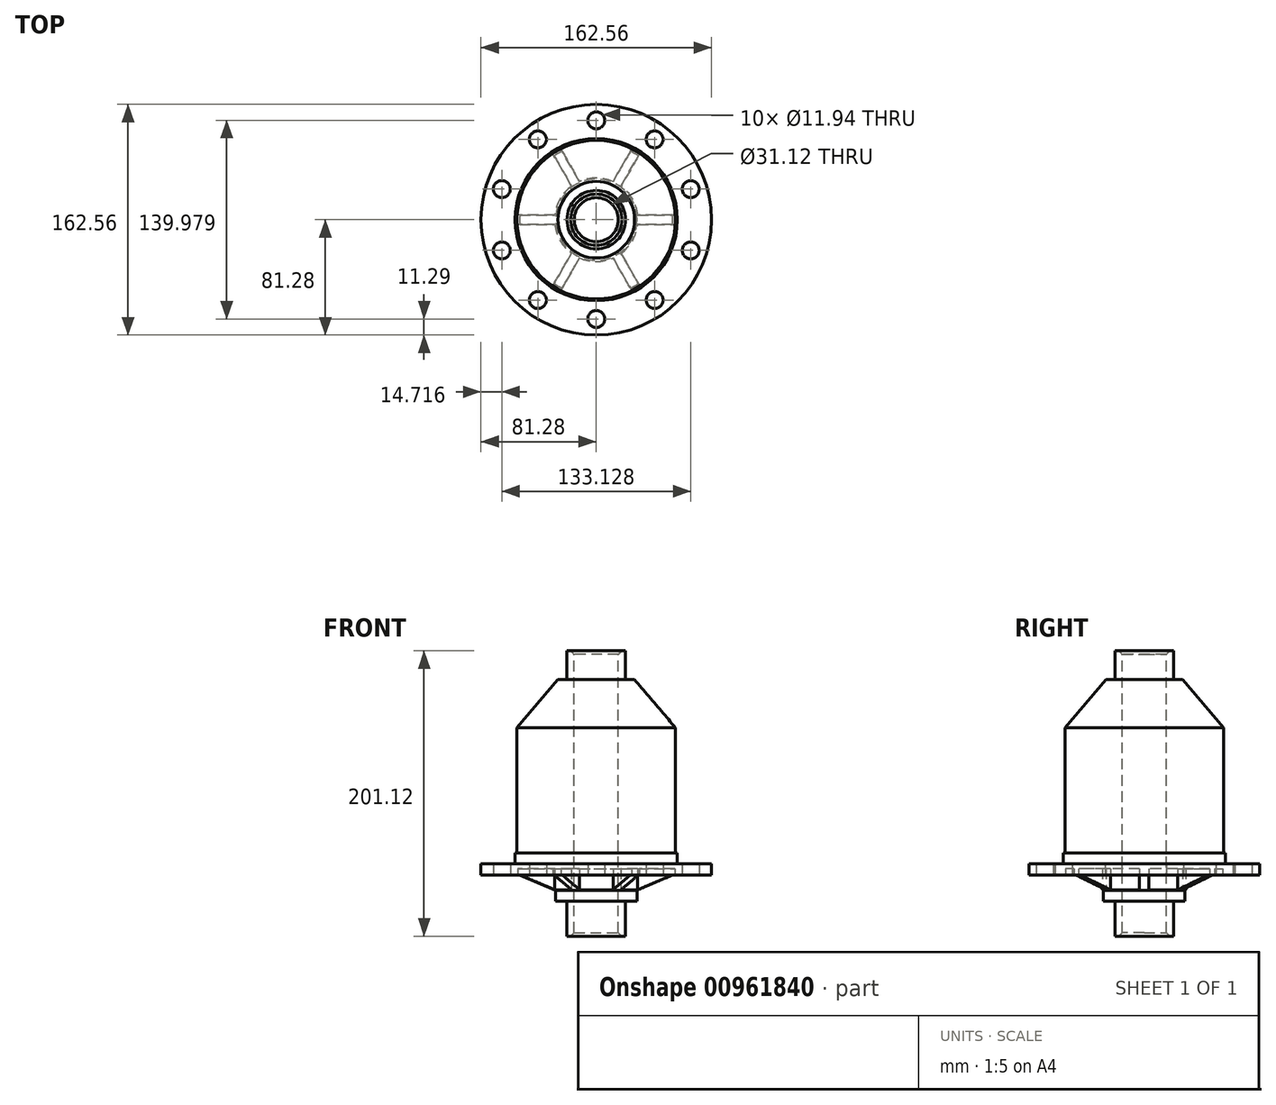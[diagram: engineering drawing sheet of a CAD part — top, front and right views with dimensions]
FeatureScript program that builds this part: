
annotation { "Feature Type Name" : "Feature", "Feature Type Description" : "" }
export const myFeature = defineFeature(function(context is Context, id is Id, definition is map)
    precondition{}
    {
        {
            var Q0;
            Q0=qCreatedBy(makeId("Front.planeOp"),FACE);
            var sketch = newSketch(context, id + "F0", { "sketchPlane" : qUnion([Q0])});
            skLineSegment(sketch, "E0", {"start": v(0, 99.57) * mm, "end": v(0, -97.81) * mm, "construction": true});
            skLineSegment(sketch, "E1", {"start": v(0, 0) * mm, "end": v(20.64, 0) * mm, "construction": true});
            skLineSegment(sketch, "E2", {"start": v(20.64, 0) * mm, "end": v(20.64, 24.77) * mm});
            skLineSegment(sketch, "E3", {"start": v(20.64, 24.77) * mm, "end": v(28.66, 24.77) * mm});
            skPoint(sketch, "E4.orphan", {"position": v(0, 24.77) * mm});
            skLineSegment(sketch, "E5", {"start": v(28.66, 24.77) * mm, "end": v(28.66, 32.39) * mm});
            skLineSegment(sketch, "E6", {"start": v(81.28, 43.18) * mm, "end": v(53.98, 43.18) * mm});
            skLineSegment(sketch, "E7", {"start": v(28.66, 32.38) * mm, "end": v(53.98, 43.18) * mm});
            skLineSegment(sketch, "E8", {"start": v(81.28, 43.18) * mm, "end": v(81.28, 51.1) * mm});
            skLineSegment(sketch, "E9", {"start": v(20.64, 0) * mm, "end": v(15.56, 0) * mm});
            skLineSegment(sketch, "E10", {"start": v(81.28, 51.1) * mm, "end": v(15.55, 51.1) * mm, "construction": true});
            skLineSegment(sketch, "E11", {"start": v(15.56, 0) * mm, "end": v(15.56, 201.12) * mm});
            skLineSegment(sketch, "E12", {"start": v(15.56, 201.12) * mm, "end": v(20.64, 201.12) * mm});
            skLineSegment(sketch, "E13", {"start": v(20.64, 201.12) * mm, "end": v(20.64, 180.8) * mm});
            skLineSegment(sketch, "E14", {"start": v(20.64, 180.8) * mm, "end": v(26.99, 180.8) * mm});
            skPoint(sketch, "E15.orphan", {"position": v(0, 51.1) * mm});
            skPoint(sketch, "E16.orphan", {"position": v(15.56, 51.1) * mm});
            skLineSegment(sketch, "E17", {"start": v(81.28, 51.1) * mm, "end": v(57.15, 51.1) * mm});
            skLineSegment(sketch, "E18", {"start": v(57.15, 51.1) * mm, "end": v(57.15, 58.72) * mm});
            skLineSegment(sketch, "E19", {"start": v(57.15, 58.72) * mm, "end": v(55.88, 58.72) * mm});
            skLineSegment(sketch, "E20", {"start": v(55.88, 58.72) * mm, "end": v(55.88, 146.87) * mm});
            skLineSegment(sketch, "E21", {"start": v(26.99, 180.8) * mm, "end": v(55.88, 146.87) * mm});
            skSolve(sketch);
        }
        {
            var Q0;
            Q0 = qSketchRegion(id + "F0", true);
            var Q1;
            Q1=sQuery(id+"F0.wireOp",EDGE,"E0");
            revolve(context, id + "F1", {"surfaceOperationType" : NewSurfaceOperationType.NEW, "entities" : qUnion([Q0]), "axis" : qUnion([Q1]), "revolveType" : RevolveType.FULL});
        }
        {
            var Q0;
            Q0=makeQuery(id+"F1.opRevolve","SWEPT_FACE",FACE,{"disambiguationData":[OSD([sQuery(id+"F0.wireOp",EDGE,"E11")])]});
            chamfer(context, id + "F2", {"entities" : qUnion([Q0]), "width" : 2.54 * mm, "tangentPropagation" : true});
        }
        {
            var Q0;
            Q0=makeQuery(id+"F1.opRevolve","SWEPT_FACE",FACE,{"disambiguationData":[OSD([sQuery(id+"F0.wireOp",EDGE,"E6")])]});
            cPlane(context, id + "F3", {"entities" : qUnion([Q0]), "cplaneType" : CPlaneType.OFFSET, "offset" : 18.41 * mm, "width" : 152.4 * mm, "height" : 152.4 * mm});
        }
        {
            var Q0;
            Q0=qCreatedBy(id+"F3.planeOp",FACE);
            var sketch = newSketch(context, id + "F4", { "sketchPlane" : qUnion([Q0])});
            skLineSegment(sketch, "E22", {"start": v(0, 113.22) * mm, "end": v(0, -117.46) * mm, "construction": true});
            skPoint(sketch, "E23.middle", {"position": v(0, 0) * mm});
            skCircle(sketch, "E24", {"center": v(0, 0) * mm, "radius": 29.41 * mm});
            skCircle(sketch, "E25", {"center": v(0, 0) * mm, "radius": 55.39 * mm});
            skLineSegment(sketch, "E26.0", {"start": v(-29.23, 3.26) * mm, "end": v(-55.3, 3.26) * mm});
            skLineSegment(sketch, "E27.MirrorCS", {"start": v(-29.23, -3.26) * mm, "end": v(-55.3, -3.26) * mm});
            skLineSegment(sketch, "E28.1.0", {"start": v(-17.44, -23.69) * mm, "end": v(-30.47, -46.26) * mm});
            skLineSegment(sketch, "E28.1.1", {"start": v(-11.8, -26.95) * mm, "end": v(-24.82, -49.51) * mm});
            skLineSegment(sketch, "E28.2.0", {"start": v(11.8, -26.95) * mm, "end": v(24.82, -49.51) * mm});
            skLineSegment(sketch, "E28.2.1", {"start": v(17.44, -23.69) * mm, "end": v(30.47, -46.26) * mm});
            skLineSegment(sketch, "E28.3.0", {"start": v(29.23, -3.26) * mm, "end": v(55.3, -3.26) * mm});
            skLineSegment(sketch, "E28.3.1", {"start": v(29.23, 3.26) * mm, "end": v(55.3, 3.26) * mm});
            skLineSegment(sketch, "E28.4.0", {"start": v(17.44, 23.69) * mm, "end": v(30.47, 46.26) * mm});
            skLineSegment(sketch, "E28.4.1", {"start": v(11.8, 26.95) * mm, "end": v(24.82, 49.51) * mm});
            skLineSegment(sketch, "E28.5.0", {"start": v(-11.8, 26.95) * mm, "end": v(-24.82, 49.51) * mm});
            skLineSegment(sketch, "E28.5.1", {"start": v(-17.44, 23.69) * mm, "end": v(-30.47, 46.26) * mm});
            skCircle(sketch, "E29", {"center": v(0, 0) * mm, "radius": 69.99 * mm, "construction": true});
            skCircle(sketch, "E30", {"center": v(0, 69.99) * mm, "radius": 5.97 * mm});
            skCircle(sketch, "E31.1.0", {"center": v(-41.14, 56.62) * mm, "radius": 5.97 * mm});
            skCircle(sketch, "E31.2.0", {"center": v(-66.56, 21.63) * mm, "radius": 5.97 * mm});
            skCircle(sketch, "E31.3.0", {"center": v(-66.56, -21.63) * mm, "radius": 5.97 * mm});
            skCircle(sketch, "E31.4.0", {"center": v(-41.14, -56.62) * mm, "radius": 5.97 * mm});
            skCircle(sketch, "E31.5.0", {"center": v(0, -69.99) * mm, "radius": 5.97 * mm});
            skCircle(sketch, "E31.6.0", {"center": v(41.14, -56.62) * mm, "radius": 5.97 * mm});
            skCircle(sketch, "E31.7.0", {"center": v(66.56, -21.63) * mm, "radius": 5.97 * mm});
            skCircle(sketch, "E31.8.0", {"center": v(66.56, 21.63) * mm, "radius": 5.97 * mm});
            skCircle(sketch, "E31.9.0", {"center": v(41.14, 56.62) * mm, "radius": 5.97 * mm});
            skSolve(sketch);
        }
        {
            var Q0;
            {var subQ0=sQuery(id+"F4.wireOp",EDGE,"E28.3.1");Q0=makeQuery(id+"F4.imprint","IMPRINT",FACE,{"disambiguationData":[TD([[makeQuery(id+"F4.imprint","IMPRINT",EDGE,{"derivedFrom":subQ0}),1.0]])]});}
            var Q1;
            {var subQ0=sQuery(id+"F4.wireOp",EDGE,"E28.4.1");Q1=makeQuery(id+"F4.imprint","IMPRINT",FACE,{"disambiguationData":[TD([[makeQuery(id+"F4.imprint","IMPRINT",EDGE,{"derivedFrom":subQ0}),1.0]])]});}
            var Q2;
            {var subQ0=sQuery(id+"F4.wireOp",EDGE,"E26.0");Q2=makeQuery(id+"F4.imprint","IMPRINT",FACE,{"disambiguationData":[TD([[makeQuery(id+"F4.imprint","IMPRINT",EDGE,{"derivedFrom":subQ0}),-1.0]])]});}
            var Q3;
            {var subQ0=sQuery(id+"F4.wireOp",EDGE,"E27.MirrorCS");Q3=makeQuery(id+"F4.imprint","IMPRINT",FACE,{"disambiguationData":[TD([[makeQuery(id+"F4.imprint","IMPRINT",EDGE,{"derivedFrom":subQ0}),1.0]])]});}
            var Q4;
            {var subQ0=sQuery(id+"F4.wireOp",EDGE,"E28.1.1");Q4=makeQuery(id+"F4.imprint","IMPRINT",FACE,{"disambiguationData":[TD([[makeQuery(id+"F4.imprint","IMPRINT",EDGE,{"derivedFrom":subQ0}),1.0]])]});}
            var Q5;
            {var subQ0=sQuery(id+"F4.wireOp",EDGE,"E28.2.1");Q5=makeQuery(id+"F4.imprint","IMPRINT",FACE,{"disambiguationData":[TD([[makeQuery(id+"F4.imprint","IMPRINT",EDGE,{"derivedFrom":subQ0}),1.0]])]});}
            extrude(context, id + "F5", {"entities" : qUnion([Q0, Q1, Q2, Q3, Q4, Q5]), "operationType" : NewBodyOperationType.REMOVE, "oppositeDirection" : true, "depth" : 22.86 * mm, "offsetDistance" : 25.4 * mm});
        }
        {
            var Q0;
            Q0=makeQuery(id+"F4.imprint","IMPRINT",FACE,{"disambiguationData":[TD([[makeQuery(id+"F4.imprint","IMPRINT",EDGE,{"derivedFrom":sQuery(id+"F4.wireOp",EDGE,"E30")}),1.0]])]});
            var Q1;
            Q1=makeQuery(id+"F4.imprint","IMPRINT",FACE,{"disambiguationData":[TD([[makeQuery(id+"F4.imprint","IMPRINT",EDGE,{"derivedFrom":sQuery(id+"F4.wireOp",EDGE,"E31.9.0")}),1.0]])]});
            var Q2;
            Q2=makeQuery(id+"F4.imprint","IMPRINT",FACE,{"disambiguationData":[TD([[makeQuery(id+"F4.imprint","IMPRINT",EDGE,{"derivedFrom":sQuery(id+"F4.wireOp",EDGE,"E31.8.0")}),1.0]])]});
            var Q3;
            Q3=makeQuery(id+"F4.imprint","IMPRINT",FACE,{"disambiguationData":[TD([[makeQuery(id+"F4.imprint","IMPRINT",EDGE,{"derivedFrom":sQuery(id+"F4.wireOp",EDGE,"E31.7.0")}),1.0]])]});
            var Q4;
            Q4=makeQuery(id+"F4.imprint","IMPRINT",FACE,{"disambiguationData":[TD([[makeQuery(id+"F4.imprint","IMPRINT",EDGE,{"derivedFrom":sQuery(id+"F4.wireOp",EDGE,"E31.1.0")}),1.0]])]});
            var Q5;
            Q5=makeQuery(id+"F4.imprint","IMPRINT",FACE,{"disambiguationData":[TD([[makeQuery(id+"F4.imprint","IMPRINT",EDGE,{"derivedFrom":sQuery(id+"F4.wireOp",EDGE,"E31.2.0")}),1.0]])]});
            var Q6;
            Q6=makeQuery(id+"F4.imprint","IMPRINT",FACE,{"disambiguationData":[TD([[makeQuery(id+"F4.imprint","IMPRINT",EDGE,{"derivedFrom":sQuery(id+"F4.wireOp",EDGE,"E31.3.0")}),1.0]])]});
            var Q7;
            Q7=makeQuery(id+"F4.imprint","IMPRINT",FACE,{"disambiguationData":[TD([[makeQuery(id+"F4.imprint","IMPRINT",EDGE,{"derivedFrom":sQuery(id+"F4.wireOp",EDGE,"E31.4.0")}),1.0]])]});
            var Q8;
            Q8=makeQuery(id+"F4.imprint","IMPRINT",FACE,{"disambiguationData":[TD([[makeQuery(id+"F4.imprint","IMPRINT",EDGE,{"derivedFrom":sQuery(id+"F4.wireOp",EDGE,"E31.5.0")}),1.0]])]});
            var Q9;
            Q9=makeQuery(id+"F4.imprint","IMPRINT",FACE,{"disambiguationData":[TD([[makeQuery(id+"F4.imprint","IMPRINT",EDGE,{"derivedFrom":sQuery(id+"F4.wireOp",EDGE,"E31.6.0")}),1.0]])]});
            extrude(context, id + "F6", {"entities" : qUnion([Q0, Q1, Q2, Q3, Q4, Q5, Q6, Q7, Q8, Q9]), "operationType" : NewBodyOperationType.REMOVE, "endBound" : BoundingType.THROUGH_ALL, "oppositeDirection" : true, "depth" : 25.4 * mm, "offsetDistance" : 25.4 * mm});
        }
    });
